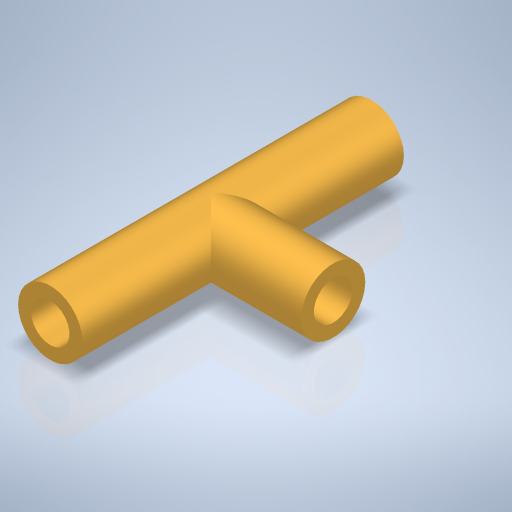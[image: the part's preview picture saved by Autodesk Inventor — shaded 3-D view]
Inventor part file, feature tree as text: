
AUTODESK INVENTOR PART (.ipt)
format: ipt  version: 2024 (Build 280153000, 153)  size: 273,408 bytes
history: native  units: mm
features: extrude x3, sketch x3, plane x1
ambient origin geometry x8: Origin, YZ Plane, XZ Plane, XY Plane, X Axis, Y Axis, Z Axis, Center Point
bodies: Volumenkörper1 (feature_tree)
feature tree (7):
  extrude  "Extrusion1"  Depth=25.0mm TaperAngle=0.0deg
  extrude  "Extrusion2"  Depth=25.0mm TaperAngle=0.0deg
  plane  "Arbeitsebene1"
  extrude  "Extrusion3"  Depth=10.0mm
  sketch  "Skizze1"  dims[d0=5.0mm d1=25.0mm d2=0.0mm]
  sketch  "Skizze2"  dims[d3=3.0mm d4=25.0mm d5=0.0mm]
  sketch  "Skizze3"  dims[d6=9.5mm d7=5.0mm d8=3.0mm d9=12.5mm d10=10.0mm d11=0.0mm]
